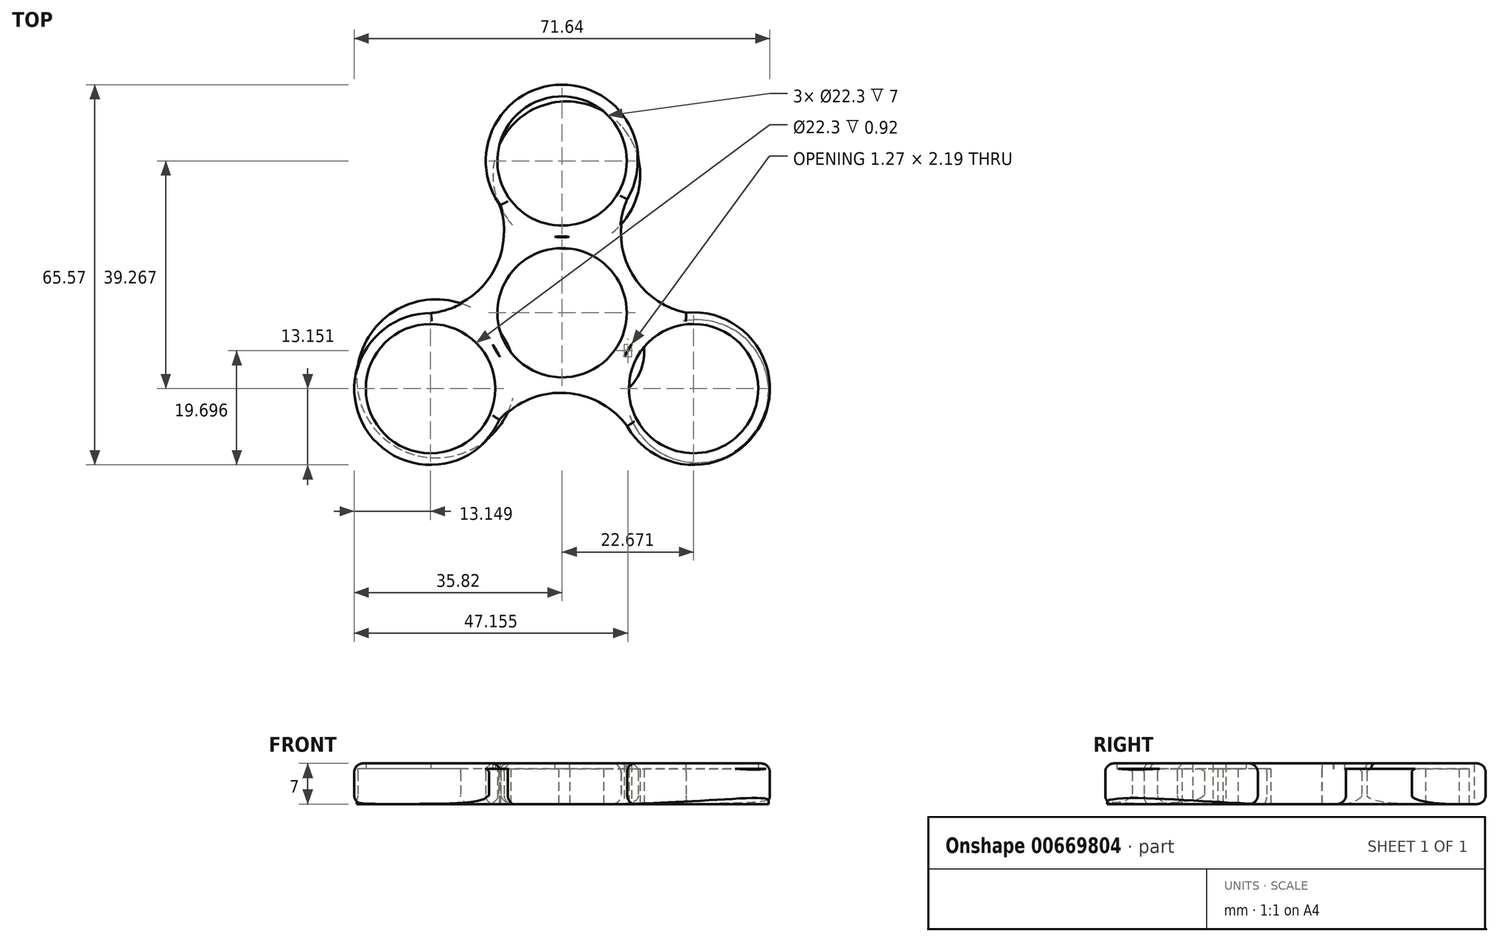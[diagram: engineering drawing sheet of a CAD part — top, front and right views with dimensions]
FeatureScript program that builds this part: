
annotation { "Feature Type Name" : "Feature", "Feature Type Description" : "" }
export const myFeature = defineFeature(function(context is Context, id is Id, definition is map)
    precondition{}
    {
        {
            var Q0;
            Q0=qCreatedBy(makeId("Top.planeOp"),FACE);
            var sketch = newSketch(context, id + "F0", { "sketchPlane" : qUnion([Q0])});
            skCircle(sketch, "E0", {"center": v(0, 0) * mm, "radius": 11.15 * mm});
            skArc(sketch, "E1", {"start": v(1.27, 13.09) * mm, "mid": v(0, 13.15) * mm, "end": v(-1.27, 13.09) * mm});
            skCircle(sketch, "E2", {"center": v(0, 26.18) * mm, "radius": 11.15 * mm});
            skArc(sketch, "E3", {"start": v(11.34, 19.51) * mm, "mid": v(-0.58, 39.31) * mm, "end": v(-10.7, 18.54) * mm});
            skArc(sketch, "E4.1.0", {"start": v(-10.7, -7.64) * mm, "mid": v(-11.28, -6.51) * mm, "end": v(-11.97, -5.45) * mm});
            skCircle(sketch, "E4.1.1", {"center": v(-22.67, -13.09) * mm, "radius": 11.15 * mm});
            skArc(sketch, "E4.2.0", {"start": v(11.23, -19.57) * mm, "mid": v(34.34, -19.15) * mm, "end": v(21.4, 0) * mm});
            skCircle(sketch, "E4.2.1", {"center": v(22.67, -13.09) * mm, "radius": 11.15 * mm});
            skArc(sketch, "E5", {"start": v(11.34, 19.51) * mm, "mid": v(11.71, 7.35) * mm, "end": v(21.4, 0) * mm});
            skArc(sketch, "E6.1.0", {"start": v(-22.57, 0.06) * mm, "mid": v(-12.23, 6.47) * mm, "end": v(-10.7, 18.54) * mm});
            skArc(sketch, "E6.2.0", {"start": v(11.23, -19.57) * mm, "mid": v(0.51, -13.82) * mm, "end": v(-10.7, -18.54) * mm});
            skArc(sketch, "E7.trimOffspring", {"start": v(-1.27, 13.09) * mm, "mid": v(0, 13.03) * mm, "end": v(1.27, 13.09) * mm});
            skArc(sketch, "E8.trimOffspring", {"start": v(10.7, -7.64) * mm, "mid": v(11.39, -6.58) * mm, "end": v(11.97, -5.45) * mm});
            skArc(sketch, "E9.trimOffspring", {"start": v(-11.97, -5.45) * mm, "mid": v(-11.39, -6.58) * mm, "end": v(-10.7, -7.64) * mm});
            skArc(sketch, "E10.trimOffspring", {"start": v(-22.57, 0.06) * mm, "mid": v(-33.76, -20.16) * mm, "end": v(-10.7, -18.54) * mm});
            skArc(sketch, "E11.trimOffspring", {"start": v(11.97, -5.45) * mm, "mid": v(11.28, -6.51) * mm, "end": v(10.7, -7.64) * mm});
            skSolve(sketch);
        }
        {
            var Q0;
            Q0=makeQuery(id+"F0.imprint","IMPRINT",FACE,{"disambiguationData":[TD([[makeQuery(id+"F0.imprint","IMPRINT",EDGE,{"derivedFrom":sQuery(id+"F0.wireOp",EDGE,"E0")}),-1.0]])]});
            extrude(context, id + "F1", {"entities" : qUnion([Q0]), "depth" : 7 * mm, "offsetDistance" : 25 * mm});
        }
        {
            var Q0;
            Q0=makeQuery(id+"F1.opExtrude","CAP_EDGE",EDGE,{"disambiguationData":[OSD([sQuery(id+"F0.wireOp",EDGE,"E10.trimOffspring")])],"isStart":false});
            var Q1;
            Q1=makeQuery(id+"F1.opExtrude","CAP_EDGE",EDGE,{"disambiguationData":[OSD([sQuery(id+"F0.wireOp",EDGE,"E6.1.0")])],"isStart":false});
            var Q2;
            Q2=makeQuery(id+"F1.opExtrude","CAP_EDGE",EDGE,{"disambiguationData":[OSD([sQuery(id+"F0.wireOp",EDGE,"E3")])],"isStart":false});
            var Q3;
            Q3=makeQuery(id+"F1.opExtrude","CAP_EDGE",EDGE,{"disambiguationData":[OSD([sQuery(id+"F0.wireOp",EDGE,"E6.2.0")])],"isStart":false});
            var Q4;
            Q4=makeQuery(id+"F1.opExtrude","CAP_EDGE",EDGE,{"disambiguationData":[OSD([sQuery(id+"F0.wireOp",EDGE,"E4.2.0")])],"isStart":false});
            var Q5;
            Q5=makeQuery(id+"F1.opExtrude","CAP_EDGE",EDGE,{"disambiguationData":[OSD([sQuery(id+"F0.wireOp",EDGE,"E5")])],"isStart":false});
            var Q6;
            Q6=makeQuery(id+"F1.opExtrude","CAP_EDGE",EDGE,{"disambiguationData":[OSD([sQuery(id+"F0.wireOp",EDGE,"E4.2.0")])],"isStart":true});
            var Q7;
            Q7=makeQuery(id+"F1.opExtrude","CAP_EDGE",EDGE,{"disambiguationData":[OSD([sQuery(id+"F0.wireOp",EDGE,"E5")])],"isStart":true});
            var Q8;
            Q8=makeQuery(id+"F1.opExtrude","CAP_EDGE",EDGE,{"disambiguationData":[OSD([sQuery(id+"F0.wireOp",EDGE,"E3")])],"isStart":true});
            var Q9;
            Q9=makeQuery(id+"F1.opExtrude","CAP_EDGE",EDGE,{"disambiguationData":[OSD([sQuery(id+"F0.wireOp",EDGE,"E6.1.0")])],"isStart":true});
            var Q10;
            Q10=makeQuery(id+"F1.opExtrude","CAP_EDGE",EDGE,{"disambiguationData":[OSD([sQuery(id+"F0.wireOp",EDGE,"E10.trimOffspring")])],"isStart":true});
            var Q11;
            Q11=makeQuery(id+"F1.opExtrude","CAP_EDGE",EDGE,{"disambiguationData":[OSD([sQuery(id+"F0.wireOp",EDGE,"E6.2.0")])],"isStart":true});
            fillet(context, id + "F2", {"entities" : qUnion([Q0, Q1, Q2, Q3, Q4, Q5, Q6, Q7, Q8, Q9, Q10, Q11]), "radius" : 1.5 * mm, "tangentPropagation" : true, "allowEdgeOverflow" : false});
        }
        {
            var Q0;
            Q0=qCreatedBy(makeId("Top.planeOp"),FACE);
            var sketch = newSketch(context, id + "F3", { "sketchPlane" : qUnion([Q0])});
            skCircle(sketch, "E12", {"center": v(23.27, -13.54) * mm, "radius": 12.34 * mm});
            skPoint(sketch, "E12.first.point", {"position": v(15, -22.7) * mm});
            skPoint(sketch, "E12.second.point", {"position": v(32.24, -5.07) * mm});
            skPoint(sketch, "E12.third.point", {"position": v(34.7, -18.2) * mm});
            skCircle(sketch, "E13", {"center": v(5.47, -6.77) * mm, "radius": 8.7 * mm});
            skPoint(sketch, "E13.first.point", {"position": v(10.93, -13.54) * mm});
            skPoint(sketch, "E13.second.point", {"position": v(0, 0) * mm});
            skPoint(sketch, "E13.third.point", {"position": v(0, -13.54) * mm});
            skCircle(sketch, "E14", {"center": v(0.77, 23.76) * mm, "radius": 12.7 * mm});
            skPoint(sketch, "E14.first.point", {"position": v(0, 11.09) * mm});
            skPoint(sketch, "E14.second.point", {"position": v(0, 36.43) * mm});
            skPoint(sketch, "E14.third.point", {"position": v(12, 29.67) * mm});
            skCircle(sketch, "E15", {"center": v(-21.72, -11.36) * mm, "radius": 13.67 * mm});
            skPoint(sketch, "E15.first.point", {"position": v(-14.11, 0) * mm});
            skPoint(sketch, "E15.second.point", {"position": v(-28.42, -23.28) * mm});
            skPoint(sketch, "E15.third.point", {"position": v(-11.8, -20.76) * mm});
            skSolve(sketch);
        }
        {
            var Q0;
            {var subQ0=sQuery(id+"F3.wireOp",EDGE,"E13");var subQ1=sQuery(id+"F3.wireOp",EDGE,"E12");var subQ2=makeQuery(id+"F3.imprint","INTERSECT",VERTEX,{"disambiguationData":[OD(0.0)],"derivedFrom":[subQ1,subQ0]});Q0=makeQuery(id+"F3.imprint","IMPRINT",FACE,{"disambiguationData":[TD([[makeQuery(id+"F3.imprint","IMPRINT",EDGE,{"disambiguationData":[TD([[subQ2,-1.0]])],"derivedFrom":subQ1}),1.0]])]});}
            var Q1;
            Q1=makeQuery(id+"F3.imprint","IMPRINT",FACE,{"disambiguationData":[TD([[makeQuery(id+"F3.imprint","IMPRINT",EDGE,{"derivedFrom":sQuery(id+"F3.wireOp",EDGE,"E14")}),1.0]])]});
            var Q2;
            Q2=makeQuery(id+"F3.imprint","IMPRINT",FACE,{"disambiguationData":[TD([[makeQuery(id+"F3.imprint","IMPRINT",EDGE,{"derivedFrom":sQuery(id+"F3.wireOp",EDGE,"E15")}),1.0]])]});
            extrude(context, id + "F4", {"entities" : qUnion([Q0, Q1, Q2]), "operationType" : NewBodyOperationType.ADD, "depth" : 6.08 * mm, "offsetDistance" : 25 * mm});
        }
    });
